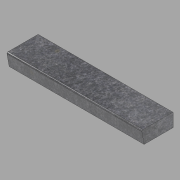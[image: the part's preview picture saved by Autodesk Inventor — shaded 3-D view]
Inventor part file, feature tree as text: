
AUTODESK INVENTOR PART (.ipt)
format: ipt  version: 2022.1 (Build 261234020, 234B)  size: 98,816 bytes
history: native  units: in
note: dims shown in document units (in); Inventor stores cm internally (conversion verified against a paired STEP export)
features: other x3, extrude x1, sketch x1
ambient origin geometry x8: Origin, YZ Plane, XZ Plane, XY Plane, X Axis, Y Axis, Z Axis, Center Point
bodies: Solid1 (feature_tree)
feature tree (5):
  other  "Blocks"
  extrude  "Extrusion1"  Depth=60.625in TaperAngle=0.0deg
  sketch  "Sketch1"  dims[d0=13.0in d1=6.0in d2=13.5in d3=0.5in d4=0.5in d5=60.625in d6=0.0in]
  other  "Profile"
  other  "Profile:1"
